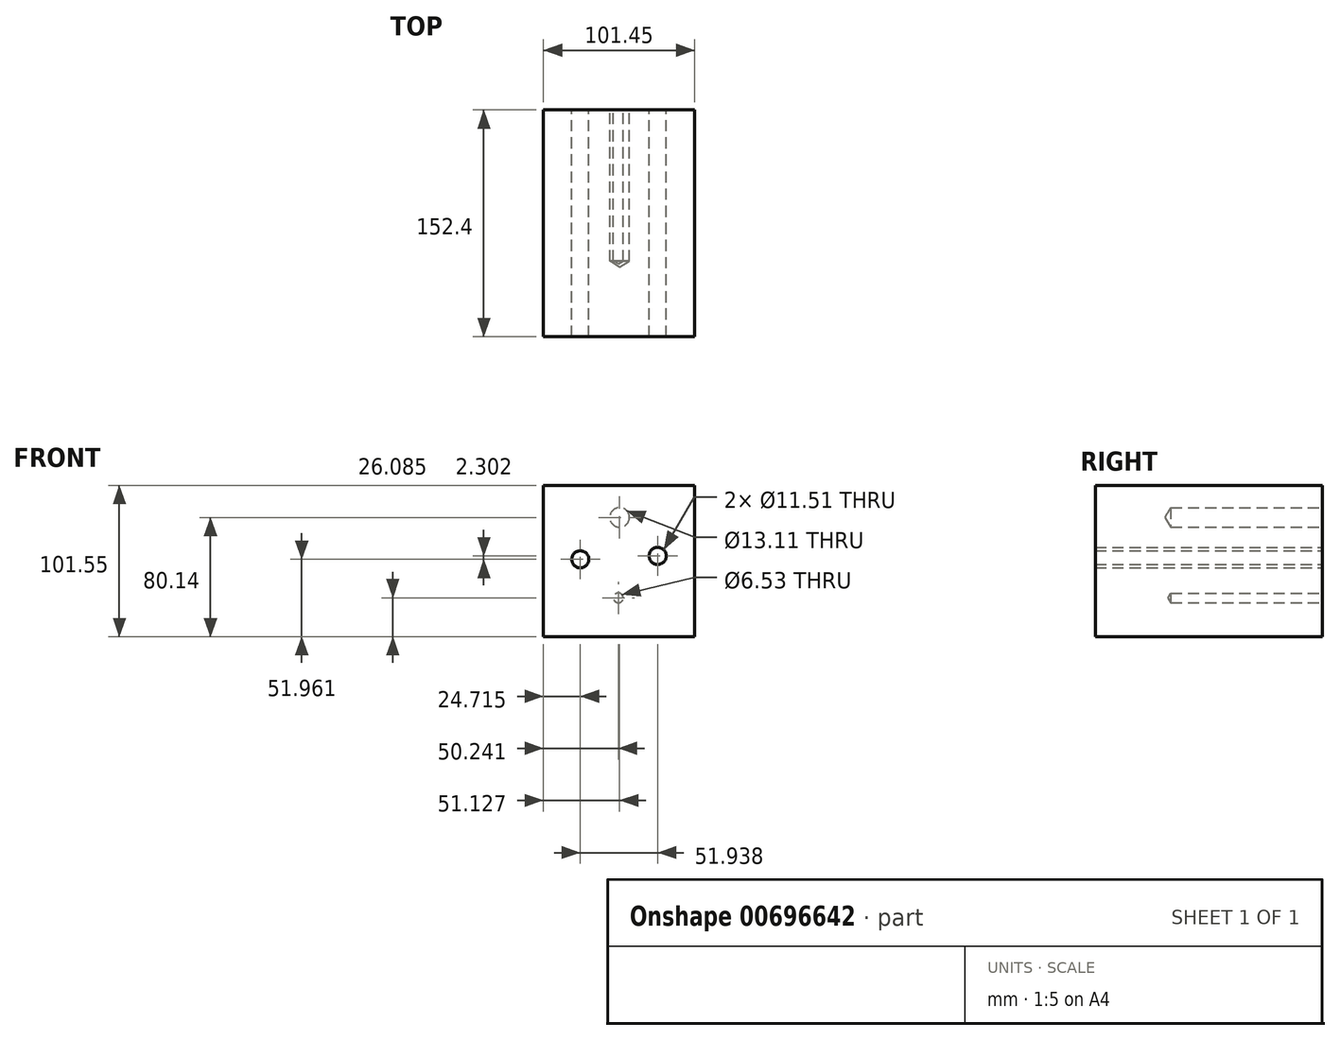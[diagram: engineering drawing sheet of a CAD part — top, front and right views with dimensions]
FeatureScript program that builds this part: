
annotation { "Feature Type Name" : "Feature", "Feature Type Description" : "" }
export const myFeature = defineFeature(function(context is Context, id is Id, definition is map)
    precondition{}
    {
        {
            var Q0;
            Q0=qCreatedBy(makeId("Front.planeOp"),FACE);
            var sketch = newSketch(context, id + "F0", { "sketchPlane" : qUnion([Q0])});
            skLineSegment(sketch, "E0.bottom", {"start": v(0, 0) * mm, "end": v(101.45, 0) * mm});
            skLineSegment(sketch, "E0.top", {"start": v(0, -101.55) * mm, "end": v(101.45, -101.55) * mm});
            skLineSegment(sketch, "E0.left", {"start": v(0, 0) * mm, "end": v(0, -101.55) * mm});
            skLineSegment(sketch, "E0.right", {"start": v(101.45, 0) * mm, "end": v(101.45, -101.55) * mm});
            skSolve(sketch);
        }
        {
            var Q0;
            Q0=makeQuery(id+"F0.imprint","IMPRINT",FACE,{"disambiguationData":[TD([[makeQuery(id+"F0.imprint","IMPRINT",EDGE,{"derivedFrom":sQuery(id+"F0.wireOp",EDGE,"E0.bottom")}),-1.0]])]});
            extrude(context, id + "F1", {"entities" : qUnion([Q0]), "depth" : 152.4 * mm, "offsetDistance" : 25.4 * mm});
        }
        {
            var Q0;
            Q0=makeQuery(id+"F1.opExtrude","CAP_FACE",FACE,{"disambiguationData":[OSD([sQuery(id+"F0.wireOp",EDGE,"E0.bottom"),sQuery(id+"F0.wireOp",EDGE,"E0.top"),sQuery(id+"F0.wireOp",EDGE,"E0.left"),sQuery(id+"F0.wireOp",EDGE,"E0.right")])],"isStart":true});
            var sketch = newSketch(context, id + "F2", { "sketchPlane" : qUnion([Q0])});
            skPoint(sketch, "E1", {"position": v(-24.72, -49.59) * mm});
            skPoint(sketch, "E2", {"position": v(-76.65, -47.29) * mm});
            skSolve(sketch);
        }
        {
            var Q0;
            Q0=makeQuery(id+"F2.imprint","IMPRINT",FACE,{"disambiguationData":[TD([[makeQuery(id+"F2.imprint","IMPRINT",EDGE,{"derivedFrom":makeQuery(id+"F1.opExtrude","CAP_EDGE",EDGE,{"disambiguationData":[OSD([sQuery(id+"F0.wireOp",EDGE,"E0.bottom")])],"isStart":true})}),1.0]])]});
            var sketch = newSketch(context, id + "F3", { "sketchPlane" : qUnion([Q0])});
            skPoint(sketch, "E3", {"position": v(-51.13, -21.4) * mm});
            skSolve(sketch);
        }
        {
            var Q0;
            Q0=makeQuery(id+"F2.imprint","IMPRINT",FACE,{"disambiguationData":[TD([[makeQuery(id+"F2.imprint","IMPRINT",EDGE,{"derivedFrom":makeQuery(id+"F1.opExtrude","CAP_EDGE",EDGE,{"disambiguationData":[OSD([sQuery(id+"F0.wireOp",EDGE,"E0.bottom")])],"isStart":true})}),1.0]])]});
            var sketch = newSketch(context, id + "F4", { "sketchPlane" : qUnion([Q0])});
            skPoint(sketch, "E4", {"position": v(-50.24, -75.47) * mm});
            skSolve(sketch);
        }
        {
            var Q0;
            Q0=sQuery(id+"F2.wireOp",VERTEX,"E2");
            var Q1;
            Q1=sQuery(id+"F2.wireOp",VERTEX,"E1");
            var Q2;
            Q2=makeQuery(id+"F1.opExtrude","SWEPT_BODY",BODY,{"disambiguationData":[OSD([sQuery(id+"F0.wireOp",EDGE,"E0.bottom"),sQuery(id+"F0.wireOp",EDGE,"E0.top"),sQuery(id+"F0.wireOp",EDGE,"E0.left"),sQuery(id+"F0.wireOp",EDGE,"E0.right")])]});
            hole(context, id + "F5", {"style" : HoleStyle.SIMPLE, "endStyle" : HoleEndStyle.THROUGH, "standardTappedOrClearance" : lookupTablePath({ "standard" : "ANSI", "engagement" : "75%", "pitch" : "20 tpi", "size" : "1/2", "type" : "Tapped" }), "standardBlindInLast" : lookupTablePath({ "standard" : "ANSI", "engagement" : "75%", "pitch" : "20 tpi", "size" : "1/2", "type" : "Tapped" }), "holeDiameter" : 11.5 * mm, "majorDiameter" : 12.7 * mm, "showTappedDepth" : true, "tappedDepth" : 72.39 * mm, "tapClearance" : 3, "startFromSketch" : true, "locations" : qUnion([Q0, Q1]), "scope" : qUnion([Q2])});
        }
        {
            var Q0;
            Q0=sQuery(id+"F3.wireOp",VERTEX,"E3");
            var Q1;
            Q1=makeQuery(id+"F1.opExtrude","SWEPT_BODY",BODY,{"disambiguationData":[OSD([sQuery(id+"F0.wireOp",EDGE,"E0.bottom"),sQuery(id+"F0.wireOp",EDGE,"E0.top"),sQuery(id+"F0.wireOp",EDGE,"E0.left"),sQuery(id+"F0.wireOp",EDGE,"E0.right")])]});
            hole(context, id + "F6", {"style" : HoleStyle.SIMPLE, "endStyle" : HoleEndStyle.BLIND, "standardTappedOrClearance" : lookupTablePath({ "standard" : "ANSI", "fit" : "Close", "size" : "1/2", "type" : "Clearance" }), "standardBlindInLast" : lookupTablePath({ "fit" : "Close", "standard" : "ANSI", "size" : "1/2", "type" : "Clearance" }), "holeDiameter" : 13.1 * mm, "majorDiameter" : 12.7 * mm, "holeDepth" : 101.6 * mm, "tappedDepth" : 72.39 * mm, "tapClearance" : 3, "startFromSketch" : true, "locations" : qUnion([Q0]), "scope" : qUnion([Q1])});
        }
        {
            var Q0;
            Q0=sQuery(id+"F4.wireOp",VERTEX,"E4");
            var Q1;
            Q1=makeQuery(id+"F1.opExtrude","SWEPT_BODY",BODY,{"disambiguationData":[OSD([sQuery(id+"F0.wireOp",EDGE,"E0.bottom"),sQuery(id+"F0.wireOp",EDGE,"E0.top"),sQuery(id+"F0.wireOp",EDGE,"E0.left"),sQuery(id+"F0.wireOp",EDGE,"E0.right")])]});
            hole(context, id + "F7", {"style" : HoleStyle.SIMPLE, "endStyle" : HoleEndStyle.BLIND, "standardTappedOrClearance" : lookupTablePath({ "standard" : "ANSI", "fit" : "Close", "size" : "1/4", "type" : "Clearance" }), "standardBlindInLast" : lookupTablePath({ "fit" : "Close", "standard" : "ANSI", "size" : "1/4", "type" : "Clearance" }), "holeDiameter" : 6.53 * mm, "majorDiameter" : 6.35 * mm, "holeDepth" : 101.6 * mm, "tappedDepth" : 72.39 * mm, "tapClearance" : 3, "startFromSketch" : true, "locations" : qUnion([Q0]), "scope" : qUnion([Q1])});
        }
    });
